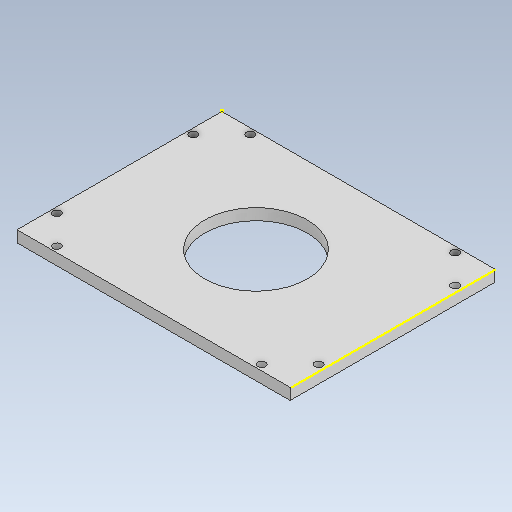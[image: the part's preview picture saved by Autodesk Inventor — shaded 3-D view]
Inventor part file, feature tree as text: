
AUTODESK INVENTOR PART (.ipt)
format: ipt  version: 2020 (Build 240168000, 168)  size: 177,152 bytes
history: native  units: mm
features: sketch x12, extrude x11
ambient origin geometry x8: Origin, YZ Plane, XZ Plane, XY Plane, X Axis, Y Axis, Z Axis, Center Point
bodies: Solid1 (feature_tree)
feature tree (23):
  extrude  "Extrusion1"  Depth=90.0mm
  extrude  "Extrusion2"  Depth=45.0mm
  extrude  "Extrusion3"  Depth=5.0mm TaperAngle=0.0deg
  extrude  "Extrusion4"  Depth=45.0mm
  extrude  "Extrusion5"  Depth=5.0mm TaperAngle=0.0deg
  extrude  "Extrusion6"  Depth=2.5mm
  extrude  "Extrusion7"  Depth=5.0mm TaperAngle=0.0deg
  extrude  "Extrusion8"  Depth=2.5mm
  extrude  "Extrusion9"  Depth=5.0mm TaperAngle=0.0deg
  sketch  "Sketch10"  dims[d22=15.0mm d23=2.5mm]
  extrude  "Extrusion10"  Depth=2.5mm
  extrude  "Extrusion11"  Depth=5.0mm
  sketch  "Sketch1"  dims[d0=120.0mm d1=90.0mm]
  sketch  "Sketch2"  dims[d2=60.0mm d3=45.0mm]
  sketch  "Sketch3"  dims[d4=45.0mm d5=5.0mm d6=0.0mm]
  sketch  "Sketch4"  dims[d7=60.0mm d8=45.0mm]
  sketch  "Sketch5"  dims[d9=45.0mm d10=5.0mm d11=0.0mm]
  sketch  "Sketch6"  dims[d12=15.0mm d13=2.5mm]
  sketch  "Sketch7"  dims[d14=3.5mm d15=5.0mm d16=0.0mm]
  sketch  "Sketch8"  dims[d17=15.0mm d18=2.5mm]
  sketch  "Sketch9"  dims[d19=3.5mm d20=5.0mm d21=0.0mm]
  sketch  "Sketch11"  dims[d25=5.0mm d26=0.0mm d27=15.0mm]
  sketch  "Sketch12"  dims[d28=2.5mm d29=3.5mm d30=5.0mm d31=0.0mm d32=3.5mm d33=15.0mm d34=2.5mm d35=3.5mm d36=5.0mm d37=0.0mm d38=2.5mm d39=15.0mm d40=3.5mm d41=10.0mm d42=0.0mm d43=2.5mm d44=15.0mm d45=3.5mm d46=10.0mm d47=0.0mm d50=2.5mm d51=15.0mm d52=3.5mm d53=10.0mm d54=0.0mm d55=2.5mm d56=15.0mm d57=3.5mm d58=10.0mm d59=0.0mm]
